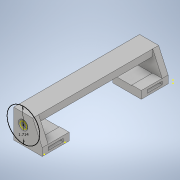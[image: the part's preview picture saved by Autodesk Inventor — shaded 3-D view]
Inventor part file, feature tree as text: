
AUTODESK INVENTOR PART (.ipt)
format: ipt  version: 2020 (Build 240168000, 168)  size: 585,728 bytes
history: native  units: in
note: dims shown in document units (in); Inventor stores cm internally (conversion verified against a paired STEP export)
features: sketch x31, extrude x20, fillet x5, hole x4
ambient origin geometry x8: Origin, YZ Plane, XZ Plane, XY Plane, X Axis, Y Axis, Z Axis, Center Point
bodies: Solid1 (feature_tree)
feature tree (60):
  sketch  "Sketch1"  dims[d6=0.3in d7=0.0in d10=1.5in d11=0.0in]
  sketch  "Sketch2"  dims[d19=0.125in d20=0.1575in d21=0.7874in]
  extrude  "Extrusion1"  Depth=1.5in TaperAngle=0.0deg
  sketch  "Sketch3"  dims[d22=0.0in d23=0.1215in]
  extrude  "Extrusion2"  Depth=0.7874in
  fillet  "Fillet1"  Radius=0.7874in
  extrude  "Extrusion3"  Depth=0.1215in
  extrude  "Extrusion4"  Depth=1.25in TaperAngle=0.0deg
  extrude  "Extrusion5"  Depth=1.25in TaperAngle=0.0deg
  hole  "Hole3"  [1 undecoded]
  hole  "Hole4"  [1 undecoded]
  hole  "Hole5"  [1 undecoded]
  extrude  "Extrusion6"  Depth=0.25in
  fillet  "Fillet2"  Radius=0.25in
  fillet  "Fillet3"  Radius=6.0in
  hole  "Hole6"  [1 undecoded]
  extrude  "Extrusion7"  Depth=0.5in TaperAngle=0.0deg
  extrude  "Extrusion8"  Depth=0.05in
  fillet  "Fillet4"  Radius=0.85in
  extrude  "Extrusion9"  Depth=0.05in
  sketch  "Sketch18"  dims[d87=0.85in d88=0.0in d89=0.05in]
  sketch  "Sketch19"  dims[d90=1.0in d91=6.6875in d92=0.0in]
  extrude  "Extrusion10"  Depth=1.0in TaperAngle=0.0deg
  extrude  "Extrusion11"  Depth=0.1181in TaperAngle=0.0deg
  sketch  "Sketch22"  dims[d98=0.325in d99=0.0in d100=1.413in]
  extrude  "Extrusion12"  Depth=0.25in
  extrude  "Extrusion13"  Depth=1.413in
  extrude  "Extrusion14"  Depth=1.413in
  extrude  "Extrusion15"  Depth=0.5in TaperAngle=0.0deg
  sketch  "Sketch27"  dims[d111=0.15in d112=0.35in d113=6.0in d114=0.0in]
  extrude  "Extrusion16"  Depth=0.125in
  extrude  "Extrusion17"  Depth=0.35in
  extrude  "Extrusion18"  Depth=0.35in
  fillet  "Fillet5"  Radius=6.0in
  extrude  "Extrusion19"  Depth=3.799in TaperAngle=0.0deg
  sketch  "Sketch32"  dims[d124=0.3125in d125=0.0in]
  extrude  "Extrusion20"  Depth=0.3125in TaperAngle=0.0deg
  sketch  "Sketch4"  dims[d24=0.1215in d25=1.25in d26=0.0in]
  sketch  "Sketch6"  dims[d28=0.0in d29=1.25in d30=0.0in]
  sketch  "Sketch7"  dims[d31=0.1215in d32=0.1215in]
  sketch  "Sketch8"  dims[d33=2.919in d35=1.25in d36=0.0in]
  sketch  "Sketch10"  dims[d37=1.25in d38=0.3125in]
  sketch  "Sketch11"  dims[d40=0.3125in d41=0.25in d42=0.25in d50=6.0in]
  sketch  "Sketch12"  dims[d51=0.35in d52=0.75in d53=0.375in d54=0.25in d55=0.5635in d56=1.0in d57=0.8108in]
  sketch  "Sketch13"  dims[d58=0.5in d59=0.75in d60=0.375in d61=0.25in d62=0.5635in d63=0.1875in d64=0.8108in]
  sketch  "Sketch14"  dims[d65=0.5in d66=0.75in d67=0.375in d68=0.25in d69=0.5635in d70=0.1875in d71=0.8108in d72=2.95in]
  sketch  "Sketch15"  dims[d73=2.95in d74=0.5in d75=0.0in]
  sketch  "Sketch16"  dims[d76=0.05in d77=0.05in]
  sketch  "Sketch17"  dims[d78=0.25in d79=0.75in d80=0.375in d81=0.25in d82=0.5635in d83=0.1875in d84=0.8108in d85=0.85in d86=0.0in]
  sketch  "Sketch20"  dims[d93=1.7143in d94=0.1181in d95=0.0in]
  sketch  "Sketch21"  dims[d96=0.25in d97=0.25in]
  sketch  "Sketch23"  dims[d101=0.401in d102=1.413in]
  sketch  "Sketch24"  dims[d103=0.401in d104=0.5in d105=0.0in]
  sketch  "Sketch25"  dims[d106=1.125in d107=0.0in d108=0.125in]
  sketch  "Sketch26"  dims[d109=0.15in d110=0.35in]
  sketch  "Sketch28"  dims[d115=3.799in d116=0.4375in d117=0.0in]
  sketch  "Sketch29"  dims[d118=0.3125in d119=0.0in d120=0.3125in d121=0.0in]
  sketch  "Sketch30"  dims[d122=0.1in]
  sketch  "Sketch31"  dims[d123=0.1in]
  sketch  "Sketch33"  dims[d126=0.1in d127=0.23in d128=0.35in d129=0.1875in d130=0.0in d131=1.0in d132=0.0in d12=1.0in d13=1.0in d14=1.0in d15=0.15in d16=0.25in d17=0.375in d18=0.5635in d133=0.5in d134=0.0344in]
note: 4 required parameter values undecoded (feature->parameter linkage not recoverable at this tier; creation-order binding heuristic only, values carry confidence <= 0.55)
